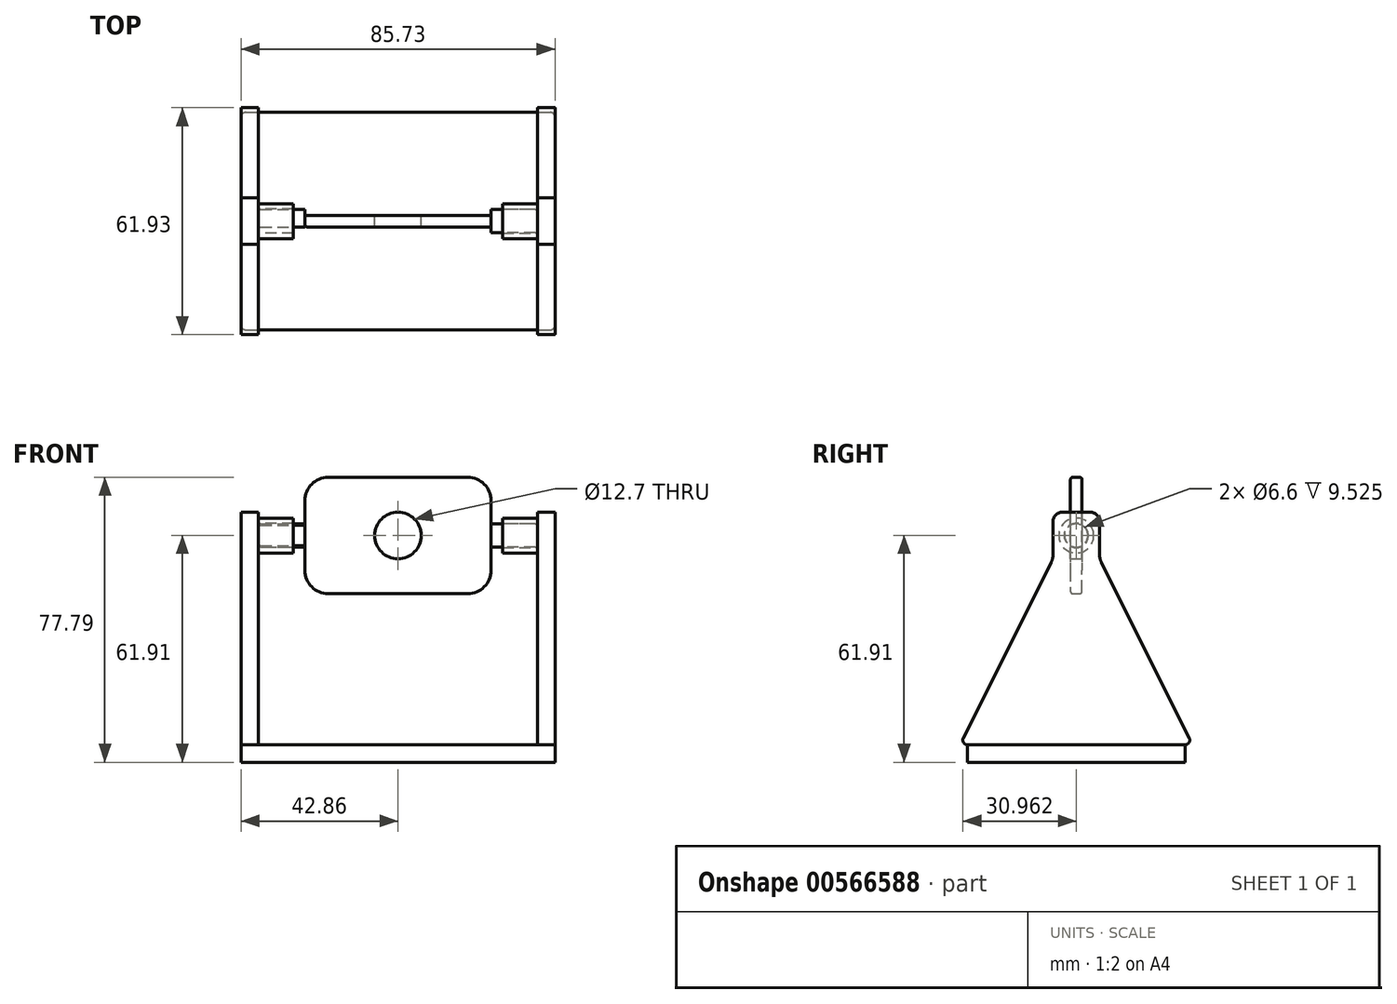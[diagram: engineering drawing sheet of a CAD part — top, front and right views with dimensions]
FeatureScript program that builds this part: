
annotation { "Feature Type Name" : "Feature", "Feature Type Description" : "" }
export const myFeature = defineFeature(function(context is Context, id is Id, definition is map)
    precondition{}
    {
        {
            var Q0;
            Q0=qCreatedBy(makeId("Front.planeOp"),FACE);
            var sketch = newSketch(context, id + "F0", { "sketchPlane" : qUnion([Q0])});
            skLineSegment(sketch, "E0.bottom", {"start": v(-38.1, 15.87) * mm, "end": v(12.7, 15.87) * mm});
            skLineSegment(sketch, "E0.top", {"start": v(-38.1, -15.87) * mm, "end": v(12.7, -15.87) * mm});
            skLineSegment(sketch, "E0.left", {"start": v(-38.1, 15.88) * mm, "end": v(-38.1, -15.87) * mm});
            skLineSegment(sketch, "E0.right", {"start": v(12.7, 15.87) * mm, "end": v(12.7, -15.88) * mm});
            skCircle(sketch, "E1", {"center": v(-12.7, 0) * mm, "radius": 6.35 * mm});
            skSolve(sketch);
        }
        {
            var Q0;
            {var subQ3=sQuery(id+"F0.wireOp",EDGE,"E0.bottom");Q0=makeQuery(id+"F0.imprint","IMPRINT",FACE,{"disambiguationData":[TD([[makeQuery(id+"F0.imprint","IMPRINT",EDGE,{"derivedFrom":subQ3}),-1.0]])]});}
            extrude(context, id + "F1", {"entities" : qUnion([Q0]), "depth" : 3.17 * mm, "offsetDistance" : 25.4 * mm});
        }
        {
            var Q0;
            Q0=makeQuery(id+"F1.opExtrude","SWEPT_FACE",FACE,{"disambiguationData":[OSD([sQuery(id+"F0.wireOp",EDGE,"E0.left")])]});
            var sketch = newSketch(context, id + "F2", { "sketchPlane" : qUnion([Q0])});
            skCircle(sketch, "E2", {"center": v(1.59, 0) * mm, "radius": 3.18 * mm});
            skPoint(sketch, "E2.centerSnap0", {"position": v(1.59, 15.88) * mm});
            skPoint(sketch, "E2.centerSnap1", {"position": v(3.18, 0) * mm});
            skSolve(sketch);
        }
        {
            var Q0;
            {var subQ0=sQuery(id+"F2.wireOp",EDGE,"E2");var subQ1=makeQuery(id+"F1.opExtrude","CAP_EDGE",EDGE,{"disambiguationData":[OSD([sQuery(id+"F0.wireOp",EDGE,"E0.left")])],"isStart":true});var subQ2=makeQuery(id+"F2.imprint","INTERSECT",VERTEX,{"disambiguationData":[OD(0.0)],"derivedFrom":[subQ1,subQ0]});Q0=makeQuery(id+"F2.imprint","IMPRINT",FACE,{"disambiguationData":[TD([[makeQuery(id+"F2.imprint","IMPRINT",EDGE,{"disambiguationData":[TD([[subQ2,-1.0]])],"derivedFrom":subQ0}),1.0]])]});}
            var Q1;
            {var subQ0=sQuery(id+"F2.wireOp",EDGE,"E2");var subQ1=sQuery(id+"F0.wireOp",EDGE,"E0.left");var subQ2=makeQuery(id+"F1.opExtrude","CAP_EDGE",EDGE,{"disambiguationData":[OSD([subQ1])],"isStart":true});var subQ3=makeQuery(id+"F2.imprint","INTERSECT",VERTEX,{"disambiguationData":[OD(0.0)],"derivedFrom":[subQ2,subQ0]});Q1=makeQuery(id+"F2.imprint","IMPRINT",FACE,{"disambiguationData":[TD([[makeQuery(id+"F2.imprint","IMPRINT",EDGE,{"disambiguationData":[TD([[subQ3,1.0]])],"derivedFrom":subQ0}),1.0]])]});}
            var Q2;
            {var subQ0=sQuery(id+"F2.wireOp",EDGE,"E2");var subQ1=makeQuery(id+"F1.opExtrude","CAP_EDGE",EDGE,{"disambiguationData":[OSD([sQuery(id+"F0.wireOp",EDGE,"E0.left")])],"isStart":false});var subQ2=makeQuery(id+"F2.imprint","INTERSECT",VERTEX,{"disambiguationData":[OD(0.0)],"derivedFrom":[subQ1,subQ0]});Q2=makeQuery(id+"F2.imprint","IMPRINT",FACE,{"disambiguationData":[TD([[makeQuery(id+"F2.imprint","IMPRINT",EDGE,{"disambiguationData":[TD([[subQ2,1.0]])],"derivedFrom":subQ0}),1.0]])]});}
            extrude(context, id + "F3", {"entities" : qUnion([Q0, Q1, Q2]), "depth" : 12.7 * mm, "offsetDistance" : 25.4 * mm});
        }
        {
            var Q0;
            Q0=makeQuery(id+"F1.opExtrude","SWEPT_FACE",FACE,{"disambiguationData":[OSD([sQuery(id+"F0.wireOp",EDGE,"E0.right"),sQuery(id+"F0.wireOp",EDGE,"f273d51c-c71d-4d26-8cfe-da776bd4fa0b.left")])]});
            var sketch = newSketch(context, id + "F4", { "sketchPlane" : qUnion([Q0])});
            skCircle(sketch, "E3", {"center": v(-1.59, 0) * mm, "radius": 3.18 * mm});
            skPoint(sketch, "E3.centerSnap0", {"position": v(-3.18, 0) * mm});
            skPoint(sketch, "E3.centerSnap1", {"position": v(-1.59, 15.87) * mm});
            skSolve(sketch);
        }
        {
            var Q0;
            {var subQ0=sQuery(id+"F4.wireOp",EDGE,"E3");var subQ1=makeQuery(id+"F1.opExtrude","CAP_EDGE",EDGE,{"disambiguationData":[OSD([sQuery(id+"F0.wireOp",EDGE,"E0.right"),sQuery(id+"F0.wireOp",EDGE,"f273d51c-c71d-4d26-8cfe-da776bd4fa0b.left")])],"isStart":false});var subQ2=makeQuery(id+"F4.imprint","INTERSECT",VERTEX,{"disambiguationData":[OD(0.0)],"derivedFrom":[subQ1,subQ0]});Q0=makeQuery(id+"F4.imprint","IMPRINT",FACE,{"disambiguationData":[TD([[makeQuery(id+"F4.imprint","IMPRINT",EDGE,{"disambiguationData":[TD([[subQ2,-1.0]])],"derivedFrom":subQ0}),1.0]])]});}
            var Q1;
            {var subQ0=sQuery(id+"F4.wireOp",EDGE,"E3");var subQ1=sQuery(id+"F0.wireOp",EDGE,"f273d51c-c71d-4d26-8cfe-da776bd4fa0b.left");var subQ2=sQuery(id+"F0.wireOp",EDGE,"E0.right");var subQ3=makeQuery(id+"F1.opExtrude","CAP_EDGE",EDGE,{"disambiguationData":[OSD([subQ2,subQ1])],"isStart":false});var subQ4=makeQuery(id+"F4.imprint","INTERSECT",VERTEX,{"disambiguationData":[OD(0.0)],"derivedFrom":[subQ3,subQ0]});Q1=makeQuery(id+"F4.imprint","IMPRINT",FACE,{"disambiguationData":[TD([[makeQuery(id+"F4.imprint","IMPRINT",EDGE,{"disambiguationData":[TD([[subQ4,1.0]])],"derivedFrom":subQ0}),1.0]])]});}
            var Q2;
            {var subQ0=sQuery(id+"F4.wireOp",EDGE,"E3");var subQ1=makeQuery(id+"F1.opExtrude","CAP_EDGE",EDGE,{"disambiguationData":[OSD([sQuery(id+"F0.wireOp",EDGE,"E0.right"),sQuery(id+"F0.wireOp",EDGE,"f273d51c-c71d-4d26-8cfe-da776bd4fa0b.left")])],"isStart":true});var subQ2=makeQuery(id+"F4.imprint","INTERSECT",VERTEX,{"disambiguationData":[OD(0.0)],"derivedFrom":[subQ1,subQ0]});Q2=makeQuery(id+"F4.imprint","IMPRINT",FACE,{"disambiguationData":[TD([[makeQuery(id+"F4.imprint","IMPRINT",EDGE,{"disambiguationData":[TD([[subQ2,1.0]])],"derivedFrom":subQ0}),1.0]])]});}
            extrude(context, id + "F5", {"entities" : qUnion([Q0, Q1, Q2]), "depth" : 12.7 * mm, "offsetDistance" : 25.4 * mm});
        }
        {
            var Q0;
            Q0=makeQuery(id+"F1.opExtrude","SWEPT_EDGE",EDGE,{"disambiguationData":[OSD([sQuery(id+"F0.wireOp",EDGE,"E0.bottom"),sQuery(id+"F0.wireOp",EDGE,"E0.left")])]});
            var Q1;
            Q1=makeQuery(id+"F1.opExtrude","SWEPT_EDGE",EDGE,{"disambiguationData":[OSD([sQuery(id+"F0.wireOp",EDGE,"E0.top"),sQuery(id+"F0.wireOp",EDGE,"E0.left")])]});
            var Q2;
            Q2=makeQuery(id+"F1.opExtrude","SWEPT_EDGE",EDGE,{"disambiguationData":[OSD([sQuery(id+"F0.wireOp",EDGE,"E0.top"),sQuery(id+"F0.wireOp",EDGE,"E0.right")])]});
            var Q3;
            Q3=makeQuery(id+"F1.opExtrude","SWEPT_EDGE",EDGE,{"disambiguationData":[OSD([sQuery(id+"F0.wireOp",EDGE,"E0.bottom"),sQuery(id+"F0.wireOp",EDGE,"E0.right")])]});
            fillet(context, id + "F6", {"entities" : qUnion([Q0, Q1, Q2, Q3]), "radius" : 6.35 * mm, "tangentPropagation" : true, "allowEdgeOverflow" : false});
        }
        {
            var Q0;
            Q0=makeQuery(id+"F1.opExtrude","CAP_EDGE",EDGE,{"disambiguationData":[OSD([sQuery(id+"F0.wireOp",EDGE,"E0.bottom")])],"isStart":false});
            fillet(context, id + "F7", {"entities" : qUnion([Q0]), "radius" : 0.64 * mm, "tangentPropagation" : true, "allowEdgeOverflow" : false});
        }
        {
            var Q0;
            Q0=makeQuery(id+"F1.opExtrude","CAP_EDGE",EDGE,{"disambiguationData":[OSD([sQuery(id+"F0.wireOp",EDGE,"E0.bottom")])],"isStart":true});
            fillet(context, id + "F8", {"entities" : qUnion([Q0]), "radius" : 0.64 * mm, "tangentPropagation" : true, "allowEdgeOverflow" : false});
        }
        {
            var Q0;
            Q0=makeQuery(id+"F3.opExtrude","CAP_EDGE",EDGE,{"disambiguationData":[OSD([sQuery(id+"F2.wireOp",EDGE,"E2")])],"isStart":false});
            var Q1;
            Q1=makeQuery(id+"F5.opExtrude","CAP_EDGE",EDGE,{"disambiguationData":[OSD([sQuery(id+"F4.wireOp",EDGE,"E3")])],"isStart":false});
            fillet(context, id + "F9", {"entities" : qUnion([Q0, Q1]), "radius" : 0.64 * mm, "tangentPropagation" : true, "allowEdgeOverflow" : false});
        }
        {
            var Q0;
            Q0=makeQuery(id+"F5.opExtrude","CAP_FACE",FACE,{"disambiguationData":[OSD([sQuery(id+"F4.wireOp",EDGE,"E3")])],"isStart":false});
            var sketch = newSketch(context, id + "F10", { "sketchPlane" : qUnion([Q0])});
            skCircle(sketch, "E4", {"center": v(-1.59, 0) * mm, "radius": 3.3 * mm});
            skCircle(sketch, "E5", {"center": v(-1.59, 0) * mm, "radius": 4.76 * mm});
            skSolve(sketch);
        }
        {
            var Q0;
            Q0=makeQuery(id+"F10.imprint","IMPRINT",FACE,{"disambiguationData":[TD([[makeQuery(id+"F10.imprint","IMPRINT",EDGE,{"derivedFrom":sQuery(id+"F10.wireOp",EDGE,"E4")}),-1.0]])]});
            extrude(context, id + "F11", {"entities" : qUnion([Q0]), "oppositeDirection" : true, "depth" : 9.52 * mm, "offsetDistance" : 25.4 * mm});
        }
        {
            var Q0;
            Q0=makeQuery(id+"F3.opExtrude","CAP_FACE",FACE,{"disambiguationData":[OSD([sQuery(id+"F2.wireOp",EDGE,"E2")])],"isStart":false});
            var sketch = newSketch(context, id + "F12", { "sketchPlane" : qUnion([Q0])});
            skCircle(sketch, "E6", {"center": v(1.59, 0) * mm, "radius": 3.3 * mm});
            skCircle(sketch, "E7", {"center": v(1.59, 0) * mm, "radius": 4.76 * mm});
            skSolve(sketch);
        }
        {
            var Q0;
            Q0=makeQuery(id+"F12.imprint","IMPRINT",FACE,{"disambiguationData":[TD([[makeQuery(id+"F12.imprint","IMPRINT",EDGE,{"derivedFrom":sQuery(id+"F12.wireOp",EDGE,"E6")}),-1.0]])]});
            extrude(context, id + "F13", {"entities" : qUnion([Q0]), "oppositeDirection" : true, "depth" : 9.52 * mm, "offsetDistance" : 25.4 * mm});
        }
        {
            var Q0;
            Q0=makeQuery(id+"F11.opExtrude","CAP_FACE",FACE,{"disambiguationData":[OSD([sQuery(id+"F10.wireOp",EDGE,"E4"),sQuery(id+"F10.wireOp",EDGE,"E5")])],"isStart":true});
            var sketch = newSketch(context, id + "F14", { "sketchPlane" : qUnion([Q0])});
            skLineSegment(sketch, "E8.bottom", {"start": v(4.76, 6.35) * mm, "end": v(-7.94, 6.35) * mm});
            skLineSegment(sketch, "E8.top", {"start": v(4.76, -6.35) * mm, "end": v(-7.94, -6.35) * mm});
            skLineSegment(sketch, "E8.left", {"start": v(4.76, 6.35) * mm, "end": v(4.76, -6.35) * mm});
            skLineSegment(sketch, "E8.right", {"start": v(-7.94, 6.35) * mm, "end": v(-7.94, -6.35) * mm});
            skPoint(sketch, "E8.middle", {"position": v(-1.59, 0) * mm});
            skLineSegment(sketch, "E9", {"start": v(-7.94, -6.35) * mm, "end": v(-33.34, -57.15) * mm});
            skLineSegment(sketch, "E10", {"start": v(4.76, -6.35) * mm, "end": v(30.16, -57.15) * mm});
            skLineSegment(sketch, "E11", {"start": v(-33.34, -57.15) * mm, "end": v(30.16, -57.15) * mm});
            skSolve(sketch);
        }
        {
            var Q0;
            Q0=makeQuery(id+"F14.imprint","IMPRINT",FACE,{"disambiguationData":[TD([[makeQuery(id+"F14.imprint","IMPRINT",EDGE,{"derivedFrom":sQuery(id+"F14.wireOp",EDGE,"E8.bottom")}),1.0]])]});
            var Q1;
            Q1=makeQuery(id+"F14.imprint","IMPRINT",FACE,{"disambiguationData":[TD([[makeQuery(id+"F14.imprint","IMPRINT",EDGE,{"derivedFrom":makeQuery(id+"F11.opExtrude","CAP_EDGE",EDGE,{"disambiguationData":[OSD([sQuery(id+"F10.wireOp",EDGE,"E4")])],"isStart":true})}),-1.0]])]});
            var Q2;
            Q2=makeQuery(id+"F14.imprint","IMPRINT",FACE,{"disambiguationData":[TD([[makeQuery(id+"F14.imprint","IMPRINT",EDGE,{"derivedFrom":makeQuery(id+"F11.opExtrude","CAP_EDGE",EDGE,{"disambiguationData":[OSD([sQuery(id+"F10.wireOp",EDGE,"E4")])],"isStart":true})}),1.0]])]});
            var Q3;
            Q3=makeQuery(id+"F14.imprint","IMPRINT",FACE,{"disambiguationData":[TD([[makeQuery(id+"F14.imprint","IMPRINT",EDGE,{"derivedFrom":sQuery(id+"F14.wireOp",EDGE,"E8.top")}),1.0]])]});
            extrude(context, id + "F15", {"entities" : qUnion([Q0, Q1, Q2, Q3]), "depth" : 4.76 * mm, "offsetDistance" : 25.4 * mm});
        }
        {
            var Q0;
            Q0=makeQuery(id+"F13.opExtrude","CAP_FACE",FACE,{"disambiguationData":[OSD([sQuery(id+"F12.wireOp",EDGE,"E6"),sQuery(id+"F12.wireOp",EDGE,"E7")])],"isStart":true});
            var sketch = newSketch(context, id + "F16", { "sketchPlane" : qUnion([Q0])});
            skLineSegment(sketch, "E12.bottom", {"start": v(7.94, 6.35) * mm, "end": v(-4.76, 6.35) * mm});
            skLineSegment(sketch, "E12.top", {"start": v(7.94, -6.35) * mm, "end": v(-4.76, -6.35) * mm});
            skLineSegment(sketch, "E12.left", {"start": v(7.94, 6.35) * mm, "end": v(7.94, -6.35) * mm});
            skLineSegment(sketch, "E12.right", {"start": v(-4.76, 6.35) * mm, "end": v(-4.76, -6.35) * mm});
            skPoint(sketch, "E12.middle", {"position": v(1.59, 0) * mm});
            skLineSegment(sketch, "E13", {"start": v(-4.76, -6.35) * mm, "end": v(-30.16, -57.15) * mm});
            skLineSegment(sketch, "E14", {"start": v(7.94, -6.35) * mm, "end": v(33.34, -57.15) * mm});
            skLineSegment(sketch, "E15", {"start": v(-30.16, -57.15) * mm, "end": v(33.34, -57.15) * mm});
            skSolve(sketch);
        }
        {
            var Q0;
            Q0=makeQuery(id+"F16.imprint","IMPRINT",FACE,{"disambiguationData":[TD([[makeQuery(id+"F16.imprint","IMPRINT",EDGE,{"derivedFrom":sQuery(id+"F16.wireOp",EDGE,"E12.bottom")}),1.0]])]});
            var Q1;
            Q1=makeQuery(id+"F16.imprint","IMPRINT",FACE,{"disambiguationData":[TD([[makeQuery(id+"F16.imprint","IMPRINT",EDGE,{"derivedFrom":makeQuery(id+"F13.opExtrude","CAP_EDGE",EDGE,{"disambiguationData":[OSD([sQuery(id+"F12.wireOp",EDGE,"E6")])],"isStart":true})}),-1.0]])]});
            var Q2;
            Q2=makeQuery(id+"F16.imprint","IMPRINT",FACE,{"disambiguationData":[TD([[makeQuery(id+"F16.imprint","IMPRINT",EDGE,{"derivedFrom":makeQuery(id+"F13.opExtrude","CAP_EDGE",EDGE,{"disambiguationData":[OSD([sQuery(id+"F12.wireOp",EDGE,"E6")])],"isStart":true})}),1.0]])]});
            var Q3;
            Q3=makeQuery(id+"F16.imprint","IMPRINT",FACE,{"disambiguationData":[TD([[makeQuery(id+"F16.imprint","IMPRINT",EDGE,{"derivedFrom":sQuery(id+"F16.wireOp",EDGE,"E12.top")}),1.0]])]});
            extrude(context, id + "F17", {"entities" : qUnion([Q0, Q1, Q2, Q3]), "depth" : 4.76 * mm, "offsetDistance" : 25.4 * mm});
        }
        {
            var Q0;
            Q0=makeQuery(id+"F17.opExtrude","SWEPT_EDGE",EDGE,{"disambiguationData":[OSD([sQuery(id+"F16.wireOp",EDGE,"E12.bottom"),sQuery(id+"F16.wireOp",EDGE,"E12.left")])]});
            var Q1;
            Q1=makeQuery(id+"F17.opExtrude","SWEPT_EDGE",EDGE,{"disambiguationData":[OSD([sQuery(id+"F16.wireOp",EDGE,"E12.bottom"),sQuery(id+"F16.wireOp",EDGE,"E12.right")])]});
            var Q2;
            Q2=makeQuery(id+"F15.opExtrude","SWEPT_EDGE",EDGE,{"disambiguationData":[OSD([sQuery(id+"F14.wireOp",EDGE,"E8.bottom"),sQuery(id+"F14.wireOp",EDGE,"E8.right")])]});
            var Q3;
            Q3=makeQuery(id+"F15.opExtrude","SWEPT_EDGE",EDGE,{"disambiguationData":[OSD([sQuery(id+"F14.wireOp",EDGE,"E8.bottom"),sQuery(id+"F14.wireOp",EDGE,"E8.left")])]});
            fillet(context, id + "F18", {"entities" : qUnion([Q0, Q1, Q2, Q3]), "radius" : 2.54 * mm, "tangentPropagation" : true, "allowEdgeOverflow" : false});
        }
        {
            var Q0;
            Q0=makeQuery(id+"F17.opExtrude","SWEPT_EDGE",EDGE,{"disambiguationData":[OSD([sQuery(id+"F16.wireOp",EDGE,"E12.top"),sQuery(id+"F16.wireOp",EDGE,"E12.left"),sQuery(id+"F16.wireOp",EDGE,"E14")])]});
            var Q1;
            Q1=makeQuery(id+"F15.opExtrude","SWEPT_EDGE",EDGE,{"disambiguationData":[OSD([sQuery(id+"F14.wireOp",EDGE,"E8.top"),sQuery(id+"F14.wireOp",EDGE,"E8.right"),sQuery(id+"F14.wireOp",EDGE,"E9")])]});
            var Q2;
            Q2=makeQuery(id+"F15.opExtrude","SWEPT_EDGE",EDGE,{"disambiguationData":[OSD([sQuery(id+"F14.wireOp",EDGE,"E8.top"),sQuery(id+"F14.wireOp",EDGE,"E8.left"),sQuery(id+"F14.wireOp",EDGE,"E10")])]});
            var Q3;
            Q3=makeQuery(id+"F17.opExtrude","SWEPT_EDGE",EDGE,{"disambiguationData":[OSD([sQuery(id+"F16.wireOp",EDGE,"E12.top"),sQuery(id+"F16.wireOp",EDGE,"E12.right"),sQuery(id+"F16.wireOp",EDGE,"E13")])]});
            fillet(context, id + "F19", {"entities" : qUnion([Q0, Q1, Q2, Q3]), "radius" : 5.08 * mm, "tangentPropagation" : true, "allowEdgeOverflow" : false});
        }
        {
            var Q0;
            Q0=makeQuery(id+"F17.opExtrude","SWEPT_EDGE",EDGE,{"disambiguationData":[OSD([sQuery(id+"F16.wireOp",EDGE,"E14"),sQuery(id+"F16.wireOp",EDGE,"E15")])]});
            var Q1;
            Q1=makeQuery(id+"F15.opExtrude","SWEPT_EDGE",EDGE,{"disambiguationData":[OSD([sQuery(id+"F14.wireOp",EDGE,"E9"),sQuery(id+"F14.wireOp",EDGE,"E11")])]});
            var Q2;
            Q2=makeQuery(id+"F17.opExtrude","SWEPT_EDGE",EDGE,{"disambiguationData":[OSD([sQuery(id+"F16.wireOp",EDGE,"E13"),sQuery(id+"F16.wireOp",EDGE,"E15")])]});
            var Q3;
            Q3=makeQuery(id+"F15.opExtrude","SWEPT_EDGE",EDGE,{"disambiguationData":[OSD([sQuery(id+"F14.wireOp",EDGE,"E10"),sQuery(id+"F14.wireOp",EDGE,"E11")])]});
            fillet(context, id + "F20", {"entities" : qUnion([Q0, Q1, Q2, Q3]), "radius" : 1.27 * mm, "tangentPropagation" : true, "allowEdgeOverflow" : false});
        }
        {
            var Q0;
            Q0=makeQuery(id+"F17.opExtrude","SWEPT_FACE",FACE,{"disambiguationData":[OSD([sQuery(id+"F16.wireOp",EDGE,"E15")])]});
            var sketch = newSketch(context, id + "F21", { "sketchPlane" : qUnion([Q0])});
            skLineSegment(sketch, "E16.bottom", {"start": v(-55.56, 31.28) * mm, "end": v(30.17, 31.28) * mm});
            skLineSegment(sketch, "E16.top", {"start": v(-55.56, -28.1) * mm, "end": v(30.17, -28.1) * mm});
            skLineSegment(sketch, "E16.left", {"start": v(-55.56, 31.28) * mm, "end": v(-55.56, -28.1) * mm});
            skLineSegment(sketch, "E16.right", {"start": v(30.17, 31.28) * mm, "end": v(30.17, -28.1) * mm});
            skSolve(sketch);
        }
        {
            var Q0;
            {var subQ4=sQuery(id+"F21.wireOp",EDGE,"E16.left");Q0=makeQuery(id+"F21.imprint","IMPRINT",FACE,{"disambiguationData":[TD([[makeQuery(id+"F21.imprint","IMPRINT",EDGE,{"derivedFrom":subQ4}),-1.0]])]});}
            var Q1;
            {var subQ3=sQuery(id+"F21.wireOp",EDGE,"E16.right");Q1=makeQuery(id+"F21.imprint","IMPRINT",FACE,{"disambiguationData":[TD([[makeQuery(id+"F21.imprint","IMPRINT",EDGE,{"derivedFrom":subQ3}),-1.0]])]});}
            extrude(context, id + "F22", {"entities" : qUnion([Q0, Q1]), "depth" : 4.76 * mm, "offsetDistance" : 25.4 * mm});
        }
        {
            var Q0;
            Q0=makeQuery(id+"F22.opExtrude","SWEPT_EDGE",EDGE,{"disambiguationData":[OSD([sQuery(id+"F21.wireOp",EDGE,"E16.bottom"),sQuery(id+"F21.wireOp",EDGE,"E16.left")])]});
            var Q1;
            Q1=makeQuery(id+"F22.opExtrude","SWEPT_EDGE",EDGE,{"disambiguationData":[OSD([sQuery(id+"F16.wireOp",EDGE,"E15"),sQuery(id+"F21.wireOp",EDGE,"E16.top"),sQuery(id+"F21.wireOp",EDGE,"E16.left")])]});
            var Q2;
            Q2=makeQuery(id+"F22.opExtrude","SWEPT_EDGE",EDGE,{"disambiguationData":[OSD([sQuery(id+"F21.wireOp",EDGE,"E16.top"),sQuery(id+"F21.wireOp",EDGE,"E16.right")])]});
            var Q3;
            Q3=makeQuery(id+"F22.opExtrude","SWEPT_EDGE",EDGE,{"disambiguationData":[OSD([sQuery(id+"F21.wireOp",EDGE,"E16.bottom"),sQuery(id+"F21.wireOp",EDGE,"E16.right")])]});
            fillet(context, id + "F23", {"entities" : qUnion([Q0, Q1, Q2, Q3]), "radius" : 1.27 * mm, "tangentPropagation" : true, "allowEdgeOverflow" : false});
        }
    });
